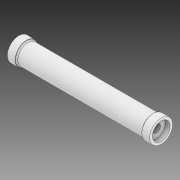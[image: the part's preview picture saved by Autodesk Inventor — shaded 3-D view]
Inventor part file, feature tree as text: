
AUTODESK INVENTOR PART (.ipt)
format: ipt  version: 2020 (Build 240168000, 168)  size: 140,288 bytes
history: native  units: mm
features: revolve x1, plane x1, mirror x1, sketch x1
ambient origin geometry x8: Origin, YZ Plane, XZ Plane, XY Plane, X Axis, Y Axis, Z Axis, Center Point
bodies: Body1 (feature_tree)
feature tree (4):
  revolve  "Revolution1"  [1 undecoded]
  plane  "Work Plane1"
  mirror  "Mirror1"
  sketch  "Sketch5"  dims[d12=5.0mm d14=6.0mm d16=11.15mm d17=14.5mm d19=10.0mm d22=90.0deg d23=0.0mm d27=80.0mm d28=1.5mm d29=12.7mm d30=3.5mm]
note: 1 required parameter value undecoded (feature->parameter linkage not recoverable at this tier; creation-order binding heuristic only, values carry confidence <= 0.55)
